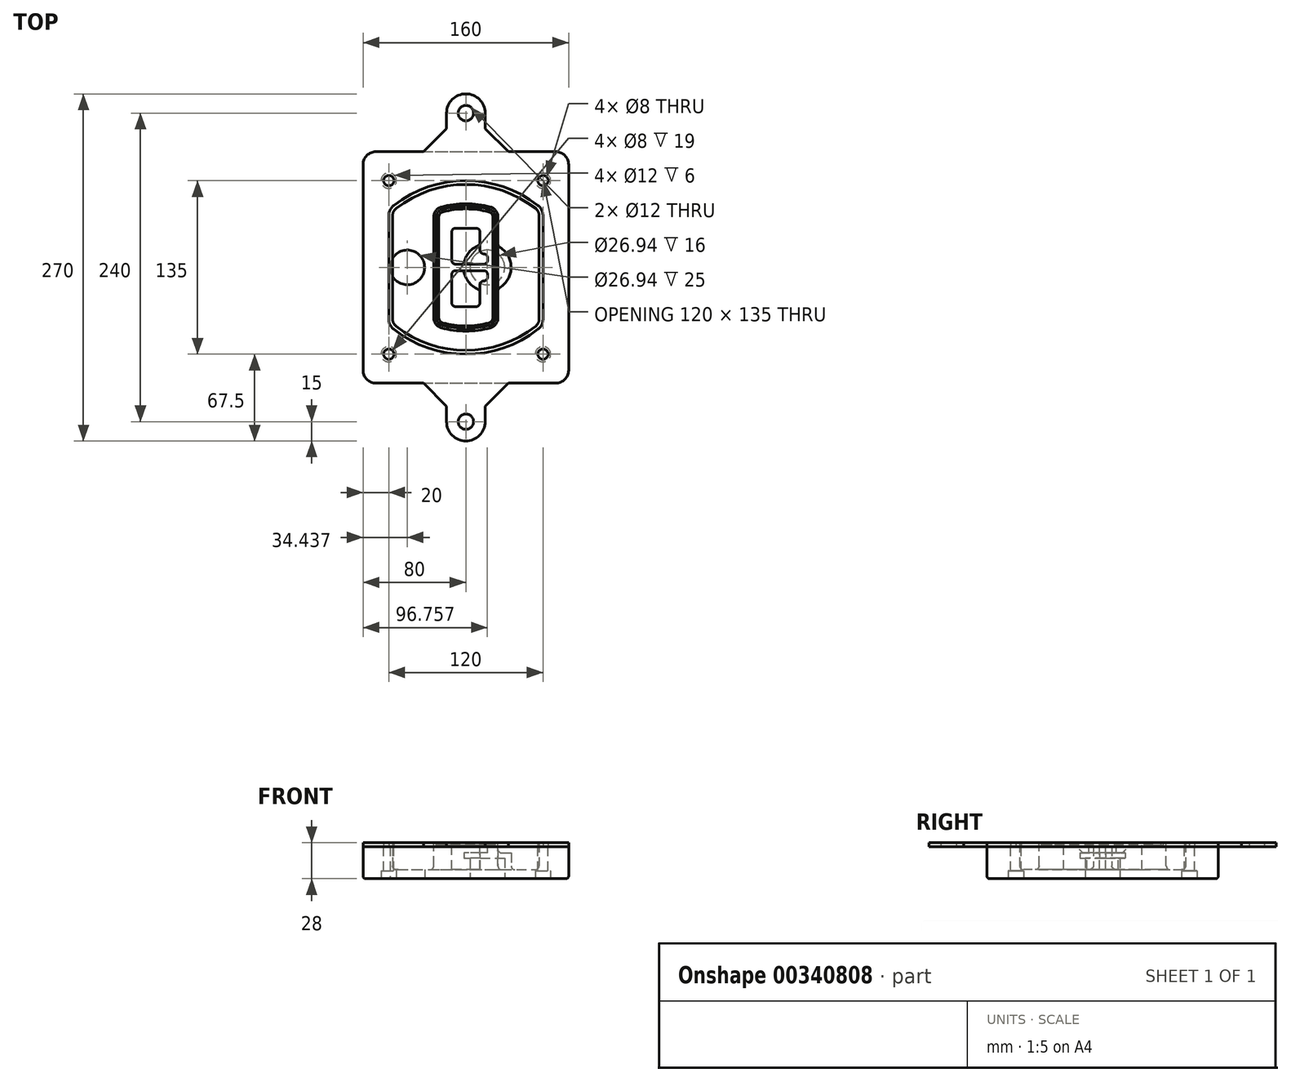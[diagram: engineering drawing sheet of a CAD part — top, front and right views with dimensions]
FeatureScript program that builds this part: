
annotation { "Feature Type Name" : "Feature", "Feature Type Description" : "" }
export const myFeature = defineFeature(function(context is Context, id is Id, definition is map)
    precondition{}
    {
        {
            var Q0;
            Q0=qCreatedBy(makeId("Top.planeOp"),FACE);
            var sketch = newSketch(context, id + "F0", { "sketchPlane" : qUnion([Q0])});
            skPoint(sketch, "E0.rect.middle", {"position": v(0, 0) * mm});
            skLineSegment(sketch, "E1.bottom", {"start": v(-70, -90) * mm, "end": v(70, -90) * mm});
            skLineSegment(sketch, "E1.top", {"start": v(-70, 90) * mm, "end": v(70, 90) * mm});
            skLineSegment(sketch, "E1.left", {"start": v(-80, -80) * mm, "end": v(-80, 80) * mm});
            skLineSegment(sketch, "E1.right", {"start": v(80, -80) * mm, "end": v(80, 80) * mm});
            skLineSegment(sketch, "E2", {"start": v(-80, 90) * mm, "end": v(80, -90) * mm, "construction": true});
            skLineSegment(sketch, "E3", {"start": v(80, 90) * mm, "end": v(-80, -90) * mm, "construction": true});
            skCircle(sketch, "E4", {"center": v(-60, 67.5) * mm, "radius": 4 * mm});
            skCircle(sketch, "E5", {"center": v(60, 67.5) * mm, "radius": 4 * mm});
            skCircle(sketch, "E6", {"center": v(60, -67.5) * mm, "radius": 4 * mm});
            skCircle(sketch, "E7", {"center": v(-60, -67.5) * mm, "radius": 4 * mm});
            skLineSegment(sketch, "E8", {"start": v(-60, 67.5) * mm, "end": v(60, 67.5) * mm, "construction": true});
            skLineSegment(sketch, "E9", {"start": v(60, 67.5) * mm, "end": v(60, -67.5) * mm, "construction": true});
            skLineSegment(sketch, "E10", {"start": v(60, -67.5) * mm, "end": v(-60, -67.5) * mm, "construction": true});
            skLineSegment(sketch, "E11", {"start": v(-60, -67.5) * mm, "end": v(-60, 67.5) * mm, "construction": true});
            skLineSegment(sketch, "E12", {"start": v(-60, 40.3) * mm, "end": v(-60, -40.3) * mm});
            skLineSegment(sketch, "E13", {"start": v(60, 40.3) * mm, "end": v(60, -40.3) * mm});
            skArc(sketch, "E14", {"start": v(56.15, 48.18) * mm, "mid": v(0, 67.5) * mm, "end": v(-56.15, 48.18) * mm});
            skArc(sketch, "E15", {"start": v(-56.15, -48.18) * mm, "mid": v(0, -67.5) * mm, "end": v(56.15, -48.18) * mm});
            skLineSegment(sketch, "E16", {"start": v(-60, 0) * mm, "end": v(60, 0) * mm, "construction": true});
            skPoint(sketch, "E17.visualSharp", {"position": v(-60, -45) * mm});
            skArc(sketch, "E17.filletArc", {"start": v(-60, -40.3) * mm, "mid": v(-58.99, -44.68) * mm, "end": v(-56.15, -48.18) * mm});
            skPoint(sketch, "E18.visualSharp", {"position": v(-60, 45) * mm});
            skArc(sketch, "E18.filletArc", {"start": v(-56.15, 48.18) * mm, "mid": v(-58.99, 44.68) * mm, "end": v(-60, 40.3) * mm});
            skPoint(sketch, "E19.visualSharp", {"position": v(60, 45) * mm});
            skArc(sketch, "E19.filletArc", {"start": v(60, 40.3) * mm, "mid": v(58.99, 44.68) * mm, "end": v(56.15, 48.18) * mm});
            skPoint(sketch, "E20.visualSharp", {"position": v(60, -45) * mm});
            skArc(sketch, "E20.filletArc", {"start": v(56.15, -48.18) * mm, "mid": v(58.99, -44.68) * mm, "end": v(60, -40.3) * mm});
            skPoint(sketch, "E21.visualSharp", {"position": v(-80, 90) * mm});
            skArc(sketch, "E21.filletArc", {"start": v(-70, 90) * mm, "mid": v(-77.07, 87.07) * mm, "end": v(-80, 80) * mm});
            skPoint(sketch, "E22.visualSharp", {"position": v(80, 90) * mm});
            skArc(sketch, "E22.filletArc", {"start": v(80, 80) * mm, "mid": v(77.07, 87.07) * mm, "end": v(70, 90) * mm});
            skPoint(sketch, "E23.visualSharp", {"position": v(80, -90) * mm});
            skArc(sketch, "E23.filletArc", {"start": v(70, -90) * mm, "mid": v(77.07, -87.07) * mm, "end": v(80, -80) * mm});
            skPoint(sketch, "E24.visualSharp", {"position": v(-80, -90) * mm});
            skArc(sketch, "E24.filletArc", {"start": v(-80, -80) * mm, "mid": v(-77.07, -87.07) * mm, "end": v(-70, -90) * mm});
            skArc(sketch, "E25.0", {"start": v(57, 40.3) * mm, "mid": v(56.3, 43.36) * mm, "end": v(54.3, 45.81) * mm});
            skLineSegment(sketch, "E25.1", {"start": v(57, 40.3) * mm, "end": v(57, -40.3) * mm});
            skArc(sketch, "E25.2", {"start": v(54.3, -45.81) * mm, "mid": v(56.3, -43.36) * mm, "end": v(57, -40.3) * mm});
            skArc(sketch, "E25.3", {"start": v(-54.3, -45.81) * mm, "mid": v(0, -64.5) * mm, "end": v(54.3, -45.81) * mm});
            skArc(sketch, "E25.4", {"start": v(-57, -40.3) * mm, "mid": v(-56.3, -43.36) * mm, "end": v(-54.3, -45.81) * mm});
            skArc(sketch, "E25.5", {"start": v(54.3, 45.81) * mm, "mid": v(0, 64.5) * mm, "end": v(-54.3, 45.81) * mm});
            skLineSegment(sketch, "E25.6", {"start": v(-57, 40.3) * mm, "end": v(-57, -40.3) * mm});
            skArc(sketch, "E25.7", {"start": v(-54.3, 45.81) * mm, "mid": v(-56.3, 43.36) * mm, "end": v(-57, 40.3) * mm});
            skArc(sketch, "E26.0", {"start": v(-58.62, 51.33) * mm, "mid": v(-62.58, 46.43) * mm, "end": v(-64, 40.3) * mm});
            skArc(sketch, "E26.1", {"start": v(58.62, 51.33) * mm, "mid": v(0, 71.5) * mm, "end": v(-58.62, 51.33) * mm});
            skArc(sketch, "E26.2", {"start": v(64, 40.3) * mm, "mid": v(62.58, 46.43) * mm, "end": v(58.62, 51.33) * mm});
            skLineSegment(sketch, "E26.3", {"start": v(64, 40.3) * mm, "end": v(64, -40.3) * mm});
            skArc(sketch, "E26.4", {"start": v(58.62, -51.33) * mm, "mid": v(62.58, -46.43) * mm, "end": v(64, -40.3) * mm});
            skLineSegment(sketch, "E26.5", {"start": v(-64, 40.3) * mm, "end": v(-64, -40.3) * mm});
            skArc(sketch, "E26.6", {"start": v(-58.62, -51.33) * mm, "mid": v(0, -71.5) * mm, "end": v(58.62, -51.33) * mm});
            skArc(sketch, "E26.7", {"start": v(-64, -40.3) * mm, "mid": v(-62.58, -46.43) * mm, "end": v(-58.62, -51.33) * mm});
            skSolve(sketch);
        }
        {
            var Q0;
            Q0=makeQuery(id+"F0.imprint","IMPRINT",FACE,{"disambiguationData":[TD([[makeQuery(id+"F0.imprint","IMPRINT",EDGE,{"derivedFrom":sQuery(id+"F0.wireOp",EDGE,"E1.bottom")}),1.0]])]});
            var Q1;
            Q1=makeQuery(id+"F0.imprint","IMPRINT",FACE,{"disambiguationData":[TD([[makeQuery(id+"F0.imprint","IMPRINT",EDGE,{"derivedFrom":sQuery(id+"F0.wireOp",EDGE,"E12")}),1.0]])]});
            var Q2;
            Q2=makeQuery(id+"F0.imprint","IMPRINT",FACE,{"disambiguationData":[TD([[makeQuery(id+"F0.imprint","IMPRINT",EDGE,{"derivedFrom":sQuery(id+"F0.wireOp",EDGE,"E25.0")}),1.0]])]});
            var Q3;
            Q3=makeQuery(id+"F0.imprint","IMPRINT",FACE,{"disambiguationData":[TD([[makeQuery(id+"F0.imprint","IMPRINT",EDGE,{"derivedFrom":sQuery(id+"F0.wireOp",EDGE,"E12")}),-1.0]])]});
            extrude(context, id + "F1", {"entities" : qUnion([Q0, Q1, Q2, Q3]), "oppositeDirection" : true, "depth" : 25 * mm});
        }
        {
            var Q0;
            Q0=makeQuery(id+"F0.imprint","IMPRINT",FACE,{"disambiguationData":[TD([[makeQuery(id+"F0.imprint","IMPRINT",EDGE,{"derivedFrom":sQuery(id+"F0.wireOp",EDGE,"E12")}),1.0]])]});
            extrude(context, id + "F2", {"entities" : qUnion([Q0]), "operationType" : NewBodyOperationType.ADD, "depth" : 3 * mm});
        }
        {
            var Q0;
            Q0=makeQuery(id+"F0.imprint","IMPRINT",FACE,{"disambiguationData":[TD([[makeQuery(id+"F0.imprint","IMPRINT",EDGE,{"derivedFrom":sQuery(id+"F0.wireOp",EDGE,"E25.0")}),1.0]])]});
            extrude(context, id + "F3", {"entities" : qUnion([Q0]), "operationType" : NewBodyOperationType.REMOVE, "oppositeDirection" : true, "depth" : 18 * mm});
        }
        {
            var Q0;
            Q0=makeQuery(id+"F2.opExtrude","CAP_FACE",FACE,{"disambiguationData":[OSD([sQuery(id+"F0.wireOp",EDGE,"E12"),sQuery(id+"F0.wireOp",EDGE,"E13"),sQuery(id+"F0.wireOp",EDGE,"E14"),sQuery(id+"F0.wireOp",EDGE,"E15"),sQuery(id+"F0.wireOp",EDGE,"E17.filletArc"),sQuery(id+"F0.wireOp",EDGE,"E18.filletArc"),sQuery(id+"F0.wireOp",EDGE,"E19.filletArc"),sQuery(id+"F0.wireOp",EDGE,"E20.filletArc"),sQuery(id+"F0.wireOp",EDGE,"E25.0"),sQuery(id+"F0.wireOp",EDGE,"E25.1"),sQuery(id+"F0.wireOp",EDGE,"E25.2"),sQuery(id+"F0.wireOp",EDGE,"E25.3"),sQuery(id+"F0.wireOp",EDGE,"E25.4"),sQuery(id+"F0.wireOp",EDGE,"E25.5"),sQuery(id+"F0.wireOp",EDGE,"E25.6"),sQuery(id+"F0.wireOp",EDGE,"E25.7")])],"isStart":false});
            var sketch = newSketch(context, id + "F4", { "sketchPlane" : qUnion([Q0])});
            skArc(sketch, "E27.0", {"start": v(-19.08, -46.97) * mm, "mid": v(0, -49.5) * mm, "end": v(19.08, -46.97) * mm});
            skArc(sketch, "E28.0", {"start": v(19.08, 46.97) * mm, "mid": v(0, 49.5) * mm, "end": v(-19.08, 46.97) * mm});
            skLineSegment(sketch, "E29", {"start": v(-25, 39.25) * mm, "end": v(-25, -39.25) * mm});
            skLineSegment(sketch, "E30", {"start": v(25, 39.25) * mm, "end": v(25, -39.25) * mm});
            skLineSegment(sketch, "E31", {"start": v(-25, 45.1) * mm, "end": v(25, 45.1) * mm, "construction": true});
            skLineSegment(sketch, "E32", {"start": v(-25, -45.1) * mm, "end": v(25, -45.1) * mm, "construction": true});
            skPoint(sketch, "E33.visualSharp", {"position": v(-25, 45.1) * mm});
            skArc(sketch, "E33.filletArc", {"start": v(-19.08, 46.97) * mm, "mid": v(-23.35, 44.11) * mm, "end": v(-25, 39.25) * mm});
            skPoint(sketch, "E34.visualSharp", {"position": v(25, 45.1) * mm});
            skArc(sketch, "E34.filletArc", {"start": v(25, 39.25) * mm, "mid": v(23.35, 44.11) * mm, "end": v(19.08, 46.97) * mm});
            skPoint(sketch, "E35.visualSharp", {"position": v(25, -45.1) * mm});
            skArc(sketch, "E35.filletArc", {"start": v(19.08, -46.97) * mm, "mid": v(23.35, -44.11) * mm, "end": v(25, -39.25) * mm});
            skPoint(sketch, "E36.visualSharp", {"position": v(-25, -45.1) * mm});
            skArc(sketch, "E36.filletArc", {"start": v(-25, -39.25) * mm, "mid": v(-23.35, -44.11) * mm, "end": v(-19.08, -46.97) * mm});
            skArc(sketch, "E37.0", {"start": v(54.3, 45.81) * mm, "mid": v(0, 64.5) * mm, "end": v(-54.3, 45.81) * mm});
            skArc(sketch, "E37.1", {"start": v(-54.3, 45.81) * mm, "mid": v(-56.3, 43.36) * mm, "end": v(-57, 40.3) * mm});
            skLineSegment(sketch, "E37.2", {"start": v(-57, 40.3) * mm, "end": v(-57, -40.3) * mm});
            skArc(sketch, "E37.3", {"start": v(-57, -40.3) * mm, "mid": v(-56.3, -43.36) * mm, "end": v(-54.3, -45.81) * mm});
            skArc(sketch, "E37.4", {"start": v(-54.3, -45.81) * mm, "mid": v(0, -64.5) * mm, "end": v(54.3, -45.81) * mm});
            skArc(sketch, "E37.5", {"start": v(54.3, -45.81) * mm, "mid": v(56.3, -43.36) * mm, "end": v(57, -40.3) * mm});
            skLineSegment(sketch, "E37.6", {"start": v(57, 40.3) * mm, "end": v(57, -40.3) * mm});
            skArc(sketch, "E37.7", {"start": v(57, 40.3) * mm, "mid": v(56.3, 43.36) * mm, "end": v(54.3, 45.81) * mm});
            skLineSegment(sketch, "E38.0", {"start": v(23, 39.25) * mm, "end": v(23, -39.25) * mm});
            skArc(sketch, "E38.1", {"start": v(18.56, -45.04) * mm, "mid": v(21.76, -42.9) * mm, "end": v(23, -39.25) * mm});
            skArc(sketch, "E38.2", {"start": v(-18.56, -45.04) * mm, "mid": v(0, -47.5) * mm, "end": v(18.56, -45.04) * mm});
            skArc(sketch, "E38.3", {"start": v(-23, -39.25) * mm, "mid": v(-21.76, -42.9) * mm, "end": v(-18.56, -45.04) * mm});
            skLineSegment(sketch, "E38.4", {"start": v(-23, 39.25) * mm, "end": v(-23, -39.25) * mm});
            skArc(sketch, "E38.5", {"start": v(23, 39.25) * mm, "mid": v(21.76, 42.9) * mm, "end": v(18.56, 45.04) * mm});
            skArc(sketch, "E38.6", {"start": v(-18.56, 45.04) * mm, "mid": v(-21.76, 42.9) * mm, "end": v(-23, 39.25) * mm});
            skArc(sketch, "E38.7", {"start": v(18.56, 45.04) * mm, "mid": v(0, 47.5) * mm, "end": v(-18.56, 45.04) * mm});
            skArc(sketch, "E39.0", {"start": v(21, 39.25) * mm, "mid": v(20.18, 41.68) * mm, "end": v(18.04, 43.1) * mm});
            skLineSegment(sketch, "E39.1", {"start": v(21, 39.25) * mm, "end": v(21, -39.25) * mm});
            skArc(sketch, "E39.2", {"start": v(18.04, -43.1) * mm, "mid": v(20.18, -41.68) * mm, "end": v(21, -39.25) * mm});
            skArc(sketch, "E39.3", {"start": v(-18.04, -43.1) * mm, "mid": v(0, -45.5) * mm, "end": v(18.04, -43.1) * mm});
            skArc(sketch, "E39.4", {"start": v(-21, -39.25) * mm, "mid": v(-20.18, -41.68) * mm, "end": v(-18.04, -43.1) * mm});
            skArc(sketch, "E39.5", {"start": v(18.04, 43.1) * mm, "mid": v(0, 45.5) * mm, "end": v(-18.04, 43.1) * mm});
            skLineSegment(sketch, "E39.6", {"start": v(-21, 39.25) * mm, "end": v(-21, -39.25) * mm});
            skArc(sketch, "E39.7", {"start": v(-18.04, 43.1) * mm, "mid": v(-20.18, 41.68) * mm, "end": v(-21, 39.25) * mm});
            skLineSegment(sketch, "E40", {"start": v(-25, 0) * mm, "end": v(25, 0) * mm, "construction": true});
            skLineSegment(sketch, "E41", {"start": v(-11, 5.5) * mm, "end": v(-11, 27.5) * mm});
            skLineSegment(sketch, "E42", {"start": v(-8, 30.5) * mm, "end": v(8, 30.5) * mm});
            skLineSegment(sketch, "E43", {"start": v(11, 27.5) * mm, "end": v(11, 13.5) * mm});
            skLineSegment(sketch, "E44", {"start": v(14, 10.5) * mm, "end": v(14, 10.5) * mm});
            skLineSegment(sketch, "E45", {"start": v(17, 7.5) * mm, "end": v(17, 5.5) * mm});
            skLineSegment(sketch, "E46", {"start": v(14, 2.5) * mm, "end": v(-8, 2.5) * mm});
            skPoint(sketch, "E47.visualSharp", {"position": v(-11, 30.5) * mm});
            skArc(sketch, "E47.filletArc", {"start": v(-8, 30.5) * mm, "mid": v(-10.12, 29.62) * mm, "end": v(-11, 27.5) * mm});
            skPoint(sketch, "E48.visualSharp", {"position": v(11, 30.5) * mm});
            skArc(sketch, "E48.filletArc", {"start": v(11, 27.5) * mm, "mid": v(10.12, 29.62) * mm, "end": v(8, 30.5) * mm});
            skPoint(sketch, "E49.visualSharp", {"position": v(11, 10.5) * mm});
            skArc(sketch, "E49.filletArc", {"start": v(11, 13.5) * mm, "mid": v(11.88, 11.38) * mm, "end": v(14, 10.5) * mm});
            skPoint(sketch, "E50.visualSharp", {"position": v(17, 10.5) * mm});
            skArc(sketch, "E50.filletArc", {"start": v(17, 7.5) * mm, "mid": v(16.12, 9.62) * mm, "end": v(14, 10.5) * mm});
            skPoint(sketch, "E51.visualSharp", {"position": v(17, 2.5) * mm});
            skArc(sketch, "E51.filletArc", {"start": v(14, 2.5) * mm, "mid": v(16.12, 3.38) * mm, "end": v(17, 5.5) * mm});
            skPoint(sketch, "E52.visualSharp", {"position": v(-11, 2.5) * mm});
            skArc(sketch, "E52.filletArc", {"start": v(-11, 5.5) * mm, "mid": v(-10.12, 3.38) * mm, "end": v(-8, 2.5) * mm});
            skLineSegment(sketch, "E53.0.MirrorCS", {"start": v(14, -2.5) * mm, "end": v(-8, -2.5) * mm});
            skArc(sketch, "E54.0.MirrorCS", {"start": v(-11, -5.5) * mm, "mid": v(-10.12, -3.38) * mm, "end": v(-8, -2.5) * mm});
            skLineSegment(sketch, "E55.0.MirrorCS", {"start": v(-11, -5.5) * mm, "end": v(-11, -27.5) * mm});
            skArc(sketch, "E56.0.MirrorCS", {"start": v(-8, -30.5) * mm, "mid": v(-10.12, -29.62) * mm, "end": v(-11, -27.5) * mm});
            skLineSegment(sketch, "E57.0.MirrorCS", {"start": v(-8, -30.5) * mm, "end": v(8, -30.5) * mm});
            skArc(sketch, "E58.0.MirrorCS", {"start": v(11, -27.5) * mm, "mid": v(10.12, -29.62) * mm, "end": v(8, -30.5) * mm});
            skLineSegment(sketch, "E59.0.MirrorCS", {"start": v(11, -27.5) * mm, "end": v(11, -13.5) * mm});
            skArc(sketch, "E60.0.MirrorCS", {"start": v(11, -13.5) * mm, "mid": v(11.88, -11.38) * mm, "end": v(14, -10.5) * mm});
            skArc(sketch, "E61.0.MirrorCS", {"start": v(17, -7.5) * mm, "mid": v(16.12, -9.62) * mm, "end": v(14, -10.5) * mm});
            skLineSegment(sketch, "E62.0.MirrorCS", {"start": v(17, -7.5) * mm, "end": v(17, -5.5) * mm});
            skArc(sketch, "E63.0.MirrorCS", {"start": v(14, -2.5) * mm, "mid": v(16.12, -3.38) * mm, "end": v(17, -5.5) * mm});
            skSolve(sketch);
        }
        {
            var Q0;
            Q0=makeQuery(id+"F4.imprint","IMPRINT",FACE,{"disambiguationData":[TD([[makeQuery(id+"F4.imprint","IMPRINT",EDGE,{"derivedFrom":sQuery(id+"F4.wireOp",EDGE,"E27.0")}),1.0]])]});
            var Q1;
            Q1=makeQuery(id+"F4.imprint","IMPRINT",FACE,{"disambiguationData":[TD([[makeQuery(id+"F4.imprint","IMPRINT",EDGE,{"derivedFrom":sQuery(id+"F4.wireOp",EDGE,"E38.0")}),-1.0]])]});
            var Q2;
            Q2=makeQuery(id+"F4.imprint","IMPRINT",FACE,{"disambiguationData":[TD([[makeQuery(id+"F4.imprint","IMPRINT",EDGE,{"derivedFrom":sQuery(id+"F4.wireOp",EDGE,"E39.0")}),1.0]])]});
            extrude(context, id + "F5", {"entities" : qUnion([Q0, Q1, Q2]), "operationType" : NewBodyOperationType.ADD, "endBound" : BoundingType.UP_TO_NEXT, "oppositeDirection" : true, "depth" : 25 * mm});
        }
        {
            var Q0;
            Q0=makeQuery(id+"F4.imprint","IMPRINT",FACE,{"disambiguationData":[TD([[makeQuery(id+"F4.imprint","IMPRINT",EDGE,{"derivedFrom":sQuery(id+"F4.wireOp",EDGE,"E38.0")}),-1.0]])]});
            extrude(context, id + "F6", {"entities" : qUnion([Q0]), "operationType" : NewBodyOperationType.REMOVE, "oppositeDirection" : true, "depth" : 2 * mm});
        }
        {
            var Q0;
            Q0=makeQuery(id+"F1.opExtrude","CAP_FACE",FACE,{"disambiguationData":[OSD([sQuery(id+"F0.wireOp",EDGE,"E1.bottom"),sQuery(id+"F0.wireOp",EDGE,"E1.top"),sQuery(id+"F0.wireOp",EDGE,"E1.left"),sQuery(id+"F0.wireOp",EDGE,"E1.right"),sQuery(id+"F0.wireOp",EDGE,"E4"),sQuery(id+"F0.wireOp",EDGE,"E5"),sQuery(id+"F0.wireOp",EDGE,"E6"),sQuery(id+"F0.wireOp",EDGE,"E7"),sQuery(id+"F0.wireOp",EDGE,"E21.filletArc"),sQuery(id+"F0.wireOp",EDGE,"E22.filletArc"),sQuery(id+"F0.wireOp",EDGE,"E23.filletArc"),sQuery(id+"F0.wireOp",EDGE,"E24.filletArc")])],"isStart":false});
            var sketch = newSketch(context, id + "F7", { "sketchPlane" : qUnion([Q0])});
            skCircle(sketch, "E64", {"center": v(16.76, 0) * mm, "radius": 13.47 * mm});
            skCircle(sketch, "E65", {"center": v(-45.56, 0) * mm, "radius": 13.47 * mm});
            skLineSegment(sketch, "E66", {"start": v(80, 0) * mm, "end": v(-80, 0) * mm});
            skCircle(sketch, "E67", {"center": v(16.76, 0) * mm, "radius": 18.47 * mm});
            skCircle(sketch, "E68", {"center": v(60, -67.5) * mm, "radius": 6 * mm});
            skCircle(sketch, "E69", {"center": v(-60, -67.5) * mm, "radius": 6 * mm});
            skCircle(sketch, "E70", {"center": v(-60, 67.5) * mm, "radius": 6 * mm});
            skCircle(sketch, "E71", {"center": v(60, 67.5) * mm, "radius": 6 * mm});
            skSolve(sketch);
        }
        {
            var Q0;
            {var subQ1=sQuery(id+"F7.wireOp",EDGE,"E66");var subQ4=sQuery(id+"F7.wireOp",EDGE,"E64");var subQ6=makeQuery(id+"F7.imprint","INTERSECT",VERTEX,{"disambiguationData":[OD(0.0)],"derivedFrom":[subQ4,subQ1]});Q0=makeQuery(id+"F7.imprint","IMPRINT",FACE,{"disambiguationData":[TD([[makeQuery(id+"F7.imprint","IMPRINT",EDGE,{"disambiguationData":[TD([[subQ6,-1.0]])],"derivedFrom":subQ4}),-1.0]])]});}
            var Q1;
            {var subQ0=sQuery(id+"F7.wireOp",EDGE,"E66");var subQ1=sQuery(id+"F7.wireOp",EDGE,"E64");var subQ3=makeQuery(id+"F7.imprint","INTERSECT",VERTEX,{"disambiguationData":[OD(0.0)],"derivedFrom":[subQ1,subQ0]});Q1=makeQuery(id+"F7.imprint","IMPRINT",FACE,{"disambiguationData":[TD([[makeQuery(id+"F7.imprint","IMPRINT",EDGE,{"disambiguationData":[TD([[subQ3,-1.0]])],"derivedFrom":subQ1}),1.0]])]});}
            var Q2;
            {var subQ0=sQuery(id+"F7.wireOp",EDGE,"E66");var subQ1=sQuery(id+"F7.wireOp",EDGE,"E64");var subQ3=makeQuery(id+"F7.imprint","INTERSECT",VERTEX,{"disambiguationData":[OD(0.0)],"derivedFrom":[subQ1,subQ0]});Q2=makeQuery(id+"F7.imprint","IMPRINT",FACE,{"disambiguationData":[TD([[makeQuery(id+"F7.imprint","IMPRINT",EDGE,{"disambiguationData":[TD([[subQ3,1.0]])],"derivedFrom":subQ1}),1.0]])]});}
            var Q3;
            {var subQ1=sQuery(id+"F7.wireOp",EDGE,"E66");var subQ4=sQuery(id+"F7.wireOp",EDGE,"E64");var subQ6=makeQuery(id+"F7.imprint","INTERSECT",VERTEX,{"disambiguationData":[OD(0.0)],"derivedFrom":[subQ4,subQ1]});Q3=makeQuery(id+"F7.imprint","IMPRINT",FACE,{"disambiguationData":[TD([[makeQuery(id+"F7.imprint","IMPRINT",EDGE,{"disambiguationData":[TD([[subQ6,1.0]])],"derivedFrom":subQ4}),-1.0]])]});}
            extrude(context, id + "F8", {"entities" : qUnion([Q0, Q1, Q2, Q3]), "operationType" : NewBodyOperationType.ADD, "oppositeDirection" : true, "depth" : 20 * mm});
        }
        {
            var Q0;
            {var subQ0=sQuery(id+"F7.wireOp",EDGE,"E66");var subQ1=sQuery(id+"F7.wireOp",EDGE,"E64");var subQ3=makeQuery(id+"F7.imprint","INTERSECT",VERTEX,{"disambiguationData":[OD(0.0)],"derivedFrom":[subQ1,subQ0]});Q0=makeQuery(id+"F7.imprint","IMPRINT",FACE,{"disambiguationData":[TD([[makeQuery(id+"F7.imprint","IMPRINT",EDGE,{"disambiguationData":[TD([[subQ3,-1.0]])],"derivedFrom":subQ1}),1.0]])]});}
            var Q1;
            {var subQ0=sQuery(id+"F7.wireOp",EDGE,"E66");var subQ1=sQuery(id+"F7.wireOp",EDGE,"E64");var subQ3=makeQuery(id+"F7.imprint","INTERSECT",VERTEX,{"disambiguationData":[OD(0.0)],"derivedFrom":[subQ1,subQ0]});Q1=makeQuery(id+"F7.imprint","IMPRINT",FACE,{"disambiguationData":[TD([[makeQuery(id+"F7.imprint","IMPRINT",EDGE,{"disambiguationData":[TD([[subQ3,1.0]])],"derivedFrom":subQ1}),1.0]])]});}
            extrude(context, id + "F9", {"entities" : qUnion([Q0, Q1]), "operationType" : NewBodyOperationType.REMOVE, "oppositeDirection" : true, "depth" : 16 * mm});
        }
        {
            var Q0;
            {var subQ0=sQuery(id+"F7.wireOp",EDGE,"E66");var subQ1=sQuery(id+"F7.wireOp",EDGE,"E65");var subQ3=makeQuery(id+"F7.imprint","INTERSECT",VERTEX,{"disambiguationData":[OD(0.0)],"derivedFrom":[subQ1,subQ0]});Q0=makeQuery(id+"F7.imprint","IMPRINT",FACE,{"disambiguationData":[TD([[makeQuery(id+"F7.imprint","IMPRINT",EDGE,{"disambiguationData":[TD([[subQ3,-1.0]])],"derivedFrom":subQ1}),1.0]])]});}
            var Q1;
            {var subQ0=sQuery(id+"F7.wireOp",EDGE,"E66");var subQ1=sQuery(id+"F7.wireOp",EDGE,"E65");var subQ3=makeQuery(id+"F7.imprint","INTERSECT",VERTEX,{"disambiguationData":[OD(0.0)],"derivedFrom":[subQ1,subQ0]});Q1=makeQuery(id+"F7.imprint","IMPRINT",FACE,{"disambiguationData":[TD([[makeQuery(id+"F7.imprint","IMPRINT",EDGE,{"disambiguationData":[TD([[subQ3,1.0]])],"derivedFrom":subQ1}),1.0]])]});}
            extrude(context, id + "F10", {"entities" : qUnion([Q0, Q1]), "operationType" : NewBodyOperationType.REMOVE, "oppositeDirection" : true, "depth" : 25 * mm});
        }
        {
            var Q0;
            Q0=makeQuery(id+"F7.imprint","IMPRINT",FACE,{"disambiguationData":[TD([[makeQuery(id+"F7.imprint","IMPRINT",EDGE,{"derivedFrom":sQuery(id+"F7.wireOp",EDGE,"E68")}),1.0]])]});
            var Q1;
            Q1=makeQuery(id+"F7.imprint","IMPRINT",FACE,{"disambiguationData":[TD([[makeQuery(id+"F7.imprint","IMPRINT",EDGE,{"derivedFrom":makeQuery(id+"F1.opExtrude","CAP_EDGE",EDGE,{"disambiguationData":[OSD([sQuery(id+"F0.wireOp",EDGE,"E5")])],"isStart":false})}),-1.0]])]});
            var Q2;
            Q2=makeQuery(id+"F7.imprint","IMPRINT",FACE,{"disambiguationData":[TD([[makeQuery(id+"F7.imprint","IMPRINT",EDGE,{"derivedFrom":sQuery(id+"F7.wireOp",EDGE,"E69")}),1.0]])]});
            var Q3;
            Q3=makeQuery(id+"F7.imprint","IMPRINT",FACE,{"disambiguationData":[TD([[makeQuery(id+"F7.imprint","IMPRINT",EDGE,{"derivedFrom":makeQuery(id+"F1.opExtrude","CAP_EDGE",EDGE,{"disambiguationData":[OSD([sQuery(id+"F0.wireOp",EDGE,"E4")])],"isStart":false})}),-1.0]])]});
            var Q4;
            Q4=makeQuery(id+"F7.imprint","IMPRINT",FACE,{"disambiguationData":[TD([[makeQuery(id+"F7.imprint","IMPRINT",EDGE,{"derivedFrom":sQuery(id+"F7.wireOp",EDGE,"E70")}),1.0]])]});
            var Q5;
            Q5=makeQuery(id+"F7.imprint","IMPRINT",FACE,{"disambiguationData":[TD([[makeQuery(id+"F7.imprint","IMPRINT",EDGE,{"derivedFrom":makeQuery(id+"F1.opExtrude","CAP_EDGE",EDGE,{"disambiguationData":[OSD([sQuery(id+"F0.wireOp",EDGE,"E7")])],"isStart":false})}),-1.0]])]});
            var Q6;
            Q6=makeQuery(id+"F7.imprint","IMPRINT",FACE,{"disambiguationData":[TD([[makeQuery(id+"F7.imprint","IMPRINT",EDGE,{"derivedFrom":sQuery(id+"F7.wireOp",EDGE,"E71")}),1.0]])]});
            var Q7;
            Q7=makeQuery(id+"F7.imprint","IMPRINT",FACE,{"disambiguationData":[TD([[makeQuery(id+"F7.imprint","IMPRINT",EDGE,{"derivedFrom":makeQuery(id+"F1.opExtrude","CAP_EDGE",EDGE,{"disambiguationData":[OSD([sQuery(id+"F0.wireOp",EDGE,"E6")])],"isStart":false})}),-1.0]])]});
            extrude(context, id + "F11", {"entities" : qUnion([Q0, Q1, Q2, Q3, Q4, Q5, Q6, Q7]), "operationType" : NewBodyOperationType.REMOVE, "oppositeDirection" : true, "depth" : 6 * mm});
        }
        {
            var Q0;
            Q0=makeQuery(id+"F9.boolean.opBoolean","COPY",FACE,{"derivedFrom":makeQuery(id+"F9.opExtrude","CAP_FACE",FACE,{"disambiguationData":[OSD([sQuery(id+"F7.wireOp",EDGE,"E64")])],"isStart":false})});
            var sketch = newSketch(context, id + "F12", { "sketchPlane" : qUnion([Q0])});
            skArc(sketch, "E72.0", {"start": v(11, 17.55) * mm, "mid": v(2.57, 11.82) * mm, "end": v(-1.54, 2.5) * mm});
            skArc(sketch, "E72.1", {"start": v(-1.54, -2.5) * mm, "mid": v(2.57, -11.82) * mm, "end": v(11, -17.55) * mm});
            skLineSegment(sketch, "E73", {"start": v(-1.54, -2.5) * mm, "end": v(14, -2.5) * mm});
            skLineSegment(sketch, "E74.0", {"start": v(14, 2.5) * mm, "end": v(-1.54, 2.5) * mm});
            skArc(sketch, "E74.1", {"start": v(14, 2.5) * mm, "mid": v(16.12, 3.38) * mm, "end": v(17, 5.5) * mm});
            skLineSegment(sketch, "E74.2", {"start": v(17, 7.5) * mm, "end": v(17, 5.5) * mm});
            skArc(sketch, "E74.3", {"start": v(17, 7.5) * mm, "mid": v(16.12, 9.62) * mm, "end": v(14, 10.5) * mm});
            skArc(sketch, "E74.4", {"start": v(11, 13.5) * mm, "mid": v(11.88, 11.38) * mm, "end": v(14, 10.5) * mm});
            skLineSegment(sketch, "E74.5", {"start": v(11, 17.55) * mm, "end": v(11, 13.5) * mm});
            skLineSegment(sketch, "E74.7", {"start": v(14, -2.5) * mm, "end": v(-1.54, -2.5) * mm});
            skArc(sketch, "E74.8", {"start": v(14, -2.5) * mm, "mid": v(16.12, -3.38) * mm, "end": v(17, -5.5) * mm});
            skLineSegment(sketch, "E74.9", {"start": v(17, -7.5) * mm, "end": v(17, -5.5) * mm});
            skArc(sketch, "E74.10", {"start": v(17, -7.5) * mm, "mid": v(16.12, -9.62) * mm, "end": v(14, -10.5) * mm});
            skArc(sketch, "E74.11", {"start": v(11, -13.5) * mm, "mid": v(11.88, -11.38) * mm, "end": v(14, -10.5) * mm});
            skLineSegment(sketch, "E74.12", {"start": v(11, -17.55) * mm, "end": v(11, -13.5) * mm});
            skPoint(sketch, "E75.orphan", {"position": v(11, -27.5) * mm});
            skPoint(sketch, "E76.orphan", {"position": v(-8, -2.5) * mm});
            skPoint(sketch, "E77.orphan", {"position": v(-8, 2.5) * mm});
            skPoint(sketch, "E78.orphan", {"position": v(11, 27.5) * mm});
            skSolve(sketch);
        }
        {
            var Q0;
            {var subQ7=sQuery(id+"F12.wireOp",EDGE,"E72.0");var subQ14=sQuery(id+"F12.wireOp",EDGE,"E72.1");var subQ16=sQuery(id+"F12.wireOp",EDGE,"E74.1");var subQ18=sQuery(id+"F12.wireOp",EDGE,"E74.8");Q0=qUnion([makeQuery(id+"F12.imprint","IMPRINT",FACE,{"disambiguationData":[TD([[makeQuery(id+"F12.imprint","IMPRINT",EDGE,{"derivedFrom":subQ7}),1.0]])]}),makeQuery(id+"F12.imprint","IMPRINT",FACE,{"disambiguationData":[TD([[makeQuery(id+"F12.imprint","IMPRINT",EDGE,{"derivedFrom":subQ14}),1.0]])]}),makeQuery(id+"F12.imprint","IMPRINT",FACE,{"disambiguationData":[TD([[makeQuery(id+"F12.imprint","IMPRINT",EDGE,{"derivedFrom":subQ16}),1.0]])]}),makeQuery(id+"F12.imprint","IMPRINT",FACE,{"disambiguationData":[TD([[makeQuery(id+"F12.imprint","IMPRINT",EDGE,{"derivedFrom":subQ18}),-1.0]])]})]);}
            var Q1;
            Q1=makeQuery(id+"F5.boolean.opBoolean","SPLIT",FACE,{"disambiguationData":[TD([makeQuery(id+"F5.opExtrude","SWEPT_FACE",FACE,{"disambiguationData":[OSD([sQuery(id+"F4.wireOp",EDGE,"E41")])]})])],"derivedFrom":makeQuery(id+"F3.boolean.opBoolean","COPY",FACE,{"derivedFrom":makeQuery(id+"F3.opExtrude","CAP_FACE",FACE,{"disambiguationData":[OSD([sQuery(id+"F0.wireOp",EDGE,"E25.0"),sQuery(id+"F0.wireOp",EDGE,"E25.1"),sQuery(id+"F0.wireOp",EDGE,"E25.2"),sQuery(id+"F0.wireOp",EDGE,"E25.3"),sQuery(id+"F0.wireOp",EDGE,"E25.4"),sQuery(id+"F0.wireOp",EDGE,"E25.5"),sQuery(id+"F0.wireOp",EDGE,"E25.6"),sQuery(id+"F0.wireOp",EDGE,"E25.7")])],"isStart":false})})});
            extrude(context, id + "F13", {"entities" : qUnion([Q0]), "operationType" : NewBodyOperationType.REMOVE, "endBound" : BoundingType.UP_TO_SURFACE, "endBoundEntityFace" : qUnion([Q1]), "depth" : 25 * mm});
        }
        {
            var Q0;
            Q0=makeQuery(id+"F3.boolean.opBoolean","COPY",EDGE,{"derivedFrom":makeQuery(id+"F3.opExtrude","CAP_EDGE",EDGE,{"disambiguationData":[OSD([sQuery(id+"F0.wireOp",EDGE,"E25.6")])],"isStart":false})});
            var Q1;
            Q1=makeQuery(id+"F8.boolean.opBoolean","INTERSECT",EDGE,{"derivedFrom":[makeQuery(id+"F5.opExtrude","SWEPT_FACE",FACE,{"disambiguationData":[OSD([sQuery(id+"F4.wireOp",EDGE,"E30")])]}),makeQuery(id+"F8.opExtrude","CAP_FACE",FACE,{"disambiguationData":[OSD([sQuery(id+"F7.wireOp",EDGE,"E67")])],"isStart":false})]});
            var Q2;
            Q2=makeQuery(id+"F8.boolean.opBoolean","INTERSECT",EDGE,{"disambiguationData":[OD(1.0)],"derivedFrom":[makeQuery(id+"F5.opExtrude","SWEPT_FACE",FACE,{"disambiguationData":[OSD([sQuery(id+"F4.wireOp",EDGE,"E30")])]}),makeQuery(id+"F8.opExtrude","SWEPT_FACE",FACE,{"disambiguationData":[OSD([sQuery(id+"F7.wireOp",EDGE,"E67")])]})]});
            var Q3;
            {var subQ0=sQuery(id+"F4.wireOp",EDGE,"E30");Q3=makeQuery(id+"F8.boolean.opBoolean","SPLIT",EDGE,{"disambiguationData":[TD([makeQuery(id+"F5.opExtrude","SWEPT_FACE",FACE,{"disambiguationData":[OSD([sQuery(id+"F4.wireOp",EDGE,"E35.filletArc")])]})])],"derivedFrom":makeQuery(id+"F5.opExtrude","CAP_EDGE",EDGE,{"disambiguationData":[OSD([subQ0])],"isStart":false})});}
            var Q4;
            {var subQ0=sQuery(id+"F0.wireOp",EDGE,"E25.7");var subQ1=sQuery(id+"F0.wireOp",EDGE,"E25.1");var subQ2=sQuery(id+"F0.wireOp",EDGE,"E25.6");var subQ3=sQuery(id+"F0.wireOp",EDGE,"E25.5");var subQ4=sQuery(id+"F0.wireOp",EDGE,"E25.4");var subQ5=sQuery(id+"F0.wireOp",EDGE,"E25.0");var subQ6=sQuery(id+"F0.wireOp",EDGE,"E25.2");var subQ7=sQuery(id+"F0.wireOp",EDGE,"E25.3");Q4=makeQuery(id+"F8.boolean.opBoolean","INTERSECT",EDGE,{"derivedFrom":[makeQuery(id+"F5.boolean.opBoolean","SPLIT",FACE,{"disambiguationData":[TD([makeQuery(id+"F2.opExtrude","SWEPT_FACE",FACE,{"disambiguationData":[OSD([subQ5])]})])],"derivedFrom":makeQuery(id+"F3.boolean.opBoolean","COPY",FACE,{"derivedFrom":makeQuery(id+"F3.opExtrude","CAP_FACE",FACE,{"disambiguationData":[OSD([subQ5,subQ1,subQ6,subQ7,subQ4,subQ3,subQ2,subQ0])],"isStart":false})})}),makeQuery(id+"F8.opExtrude","SWEPT_FACE",FACE,{"disambiguationData":[OSD([sQuery(id+"F7.wireOp",EDGE,"E67")])]})]});}
            var Q5;
            Q5=makeQuery(id+"F8.boolean.opBoolean","INTERSECT",EDGE,{"disambiguationData":[OD(0.0)],"derivedFrom":[makeQuery(id+"F5.opExtrude","SWEPT_FACE",FACE,{"disambiguationData":[OSD([sQuery(id+"F4.wireOp",EDGE,"E30")])]}),makeQuery(id+"F8.opExtrude","SWEPT_FACE",FACE,{"disambiguationData":[OSD([sQuery(id+"F7.wireOp",EDGE,"E67")])]})]});
            fillet(context, id + "F14", {"entities" : qUnion([Q0, Q1, Q2, Q3, Q4, Q5]), "radius" : 3 * mm, "tangentPropagation" : true, "allowEdgeOverflow" : false});
        }
        {
            var Q0;
            Q0=makeQuery(id+"F1.opExtrude","CAP_EDGE",EDGE,{"disambiguationData":[OSD([sQuery(id+"F0.wireOp",EDGE,"E1.bottom")])],"isStart":false});
            fillet(context, id + "F15", {"entities" : qUnion([Q0]), "radius" : 2 * mm, "tangentPropagation" : true, "allowEdgeOverflow" : false});
        }
        {
            var Q0;
            {var subQ0=sQuery(id+"F0.wireOp",EDGE,"E21.filletArc");var subQ1=sQuery(id+"F0.wireOp",EDGE,"E7");var subQ2=sQuery(id+"F0.wireOp",EDGE,"E6");var subQ3=sQuery(id+"F0.wireOp",EDGE,"E5");var subQ4=sQuery(id+"F0.wireOp",EDGE,"E4");var subQ5=sQuery(id+"F0.wireOp",EDGE,"E22.filletArc");var subQ6=sQuery(id+"F0.wireOp",EDGE,"E1.bottom");var subQ7=sQuery(id+"F0.wireOp",EDGE,"E1.right");var subQ8=sQuery(id+"F0.wireOp",EDGE,"E1.top");var subQ9=sQuery(id+"F0.wireOp",EDGE,"E1.left");var subQ10=sQuery(id+"F0.wireOp",EDGE,"E23.filletArc");var subQ11=sQuery(id+"F0.wireOp",EDGE,"E24.filletArc");Q0=makeQuery(id+"F2.boolean.opBoolean","SPLIT",FACE,{"disambiguationData":[TD([makeQuery(id+"F1.opExtrude","SWEPT_FACE",FACE,{"disambiguationData":[OSD([subQ6])]})])],"derivedFrom":makeQuery(id+"F1.opExtrude","CAP_FACE",FACE,{"disambiguationData":[OSD([subQ6,subQ8,subQ9,subQ7,subQ4,subQ3,subQ2,subQ1,subQ0,subQ5,subQ10,subQ11])],"isStart":true})});}
            var sketch = newSketch(context, id + "F16", { "sketchPlane" : qUnion([Q0])});
            skLineSegment(sketch, "E79.0", {"start": v(-80, -80) * mm, "end": v(-80, 80) * mm});
            skArc(sketch, "E79.1", {"start": v(-70, 90) * mm, "mid": v(-77.07, 87.07) * mm, "end": v(-80, 80) * mm});
            skLineSegment(sketch, "E79.2", {"start": v(-70, 90) * mm, "end": v(70, 90) * mm});
            skArc(sketch, "E79.3", {"start": v(80, 80) * mm, "mid": v(77.07, 87.07) * mm, "end": v(70, 90) * mm});
            skLineSegment(sketch, "E79.4", {"start": v(80, -80) * mm, "end": v(80, 80) * mm});
            skCircle(sketch, "E79.5", {"center": v(60, 67.5) * mm, "radius": 4 * mm});
            skArc(sketch, "E79.6", {"start": v(56.15, 48.18) * mm, "mid": v(0, 67.5) * mm, "end": v(-56.15, 48.18) * mm});
            skArc(sketch, "E79.7", {"start": v(60, 40.3) * mm, "mid": v(58.99, 44.68) * mm, "end": v(56.15, 48.18) * mm});
            skArc(sketch, "E79.8", {"start": v(-56.15, 48.18) * mm, "mid": v(-58.99, 44.68) * mm, "end": v(-60, 40.3) * mm});
            skCircle(sketch, "E79.9", {"center": v(-60, 67.5) * mm, "radius": 4 * mm});
            skLineSegment(sketch, "E79.10", {"start": v(-60, 40.3) * mm, "end": v(-60, -40.3) * mm});
            skArc(sketch, "E79.11", {"start": v(-60, -40.3) * mm, "mid": v(-58.99, -44.68) * mm, "end": v(-56.15, -48.18) * mm});
            skArc(sketch, "E79.12", {"start": v(-56.15, -48.18) * mm, "mid": v(0, -67.5) * mm, "end": v(56.15, -48.18) * mm});
            skCircle(sketch, "E79.13", {"center": v(-60, -67.5) * mm, "radius": 4 * mm});
            skArc(sketch, "E79.14", {"start": v(-80, -80) * mm, "mid": v(-77.07, -87.07) * mm, "end": v(-70, -90) * mm});
            skLineSegment(sketch, "E79.15", {"start": v(-70, -90) * mm, "end": v(70, -90) * mm});
            skCircle(sketch, "E79.16", {"center": v(60, -67.5) * mm, "radius": 4 * mm});
            skArc(sketch, "E79.17", {"start": v(70, -90) * mm, "mid": v(77.07, -87.07) * mm, "end": v(80, -80) * mm});
            skLineSegment(sketch, "E79.18", {"start": v(60, 40.3) * mm, "end": v(60, -40.3) * mm});
            skArc(sketch, "E79.19", {"start": v(56.15, -48.18) * mm, "mid": v(58.99, -44.68) * mm, "end": v(60, -40.3) * mm});
            skLineSegment(sketch, "E80", {"start": v(0, 90) * mm, "end": v(0, 120) * mm, "construction": true});
            skCircle(sketch, "E81", {"center": v(0, 120) * mm, "radius": 6 * mm});
            skLineSegment(sketch, "E82", {"start": v(-33, 90) * mm, "end": v(-15, 108) * mm});
            skLineSegment(sketch, "E83", {"start": v(-15, 108) * mm, "end": v(-15, 120) * mm});
            skLineSegment(sketch, "E84", {"start": v(33, 90) * mm, "end": v(15, 108) * mm});
            skLineSegment(sketch, "E85", {"start": v(15, 108) * mm, "end": v(15, 120) * mm});
            skArc(sketch, "E86", {"start": v(15, 120) * mm, "mid": v(0, 135) * mm, "end": v(-15, 120) * mm});
            skLineSegment(sketch, "E87", {"start": v(-80, 0) * mm, "end": v(80, 0) * mm, "construction": true});
            skCircle(sketch, "E88.MirrorC", {"center": v(0, -120) * mm, "radius": 6 * mm});
            skArc(sketch, "E89.MirrorCS", {"start": v(15, -120) * mm, "mid": v(0, -135) * mm, "end": v(-15, -120) * mm});
            skLineSegment(sketch, "E90.MirrorCS", {"start": v(-15, -108) * mm, "end": v(-15, -120) * mm});
            skLineSegment(sketch, "E91.MirrorCS", {"start": v(15, -108) * mm, "end": v(15, -120) * mm});
            skLineSegment(sketch, "E92.MirrorCS", {"start": v(-33, -90) * mm, "end": v(-15, -108) * mm});
            skLineSegment(sketch, "E93.MirrorCS", {"start": v(33, -90) * mm, "end": v(15, -108) * mm});
            skLineSegment(sketch, "E94.MirrorCS", {"start": v(0, -90) * mm, "end": v(0, -120) * mm, "construction": true});
            skSolve(sketch);
        }
        {
            var Q0;
            Q0 = qSketchRegion(id + "F16", true);
            var Q1;
            Q1=makeQuery(id+"F2.opExtrude","CAP_FACE",FACE,{"disambiguationData":[OSD([sQuery(id+"F0.wireOp",EDGE,"E12"),sQuery(id+"F0.wireOp",EDGE,"E13"),sQuery(id+"F0.wireOp",EDGE,"E14"),sQuery(id+"F0.wireOp",EDGE,"E15"),sQuery(id+"F0.wireOp",EDGE,"E17.filletArc"),sQuery(id+"F0.wireOp",EDGE,"E18.filletArc"),sQuery(id+"F0.wireOp",EDGE,"E19.filletArc"),sQuery(id+"F0.wireOp",EDGE,"E20.filletArc"),sQuery(id+"F0.wireOp",EDGE,"E25.0"),sQuery(id+"F0.wireOp",EDGE,"E25.1"),sQuery(id+"F0.wireOp",EDGE,"E25.2"),sQuery(id+"F0.wireOp",EDGE,"E25.3"),sQuery(id+"F0.wireOp",EDGE,"E25.4"),sQuery(id+"F0.wireOp",EDGE,"E25.5"),sQuery(id+"F0.wireOp",EDGE,"E25.6"),sQuery(id+"F0.wireOp",EDGE,"E25.7")])],"isStart":false});
            extrude(context, id + "F17", {"entities" : qUnion([Q0]), "endBound" : BoundingType.UP_TO_SURFACE, "endBoundEntityFace" : qUnion([Q1]), "depth" : 25 * mm});
        }
    });
